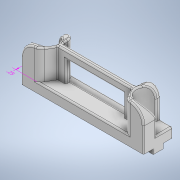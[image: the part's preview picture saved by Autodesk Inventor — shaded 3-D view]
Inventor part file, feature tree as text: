
AUTODESK INVENTOR PART (.ipt)
format: ipt  version: 2020 (Build 240168000, 168)  size: 448,512 bytes
history: native  units: in
note: dims shown in document units (in); Inventor stores cm internally (conversion verified against a paired STEP export)
features: fillet x8, sketch x6, extrude x5, other x2, hole x1
ambient origin geometry x8: Origin, YZ Plane, XZ Plane, XY Plane, X Axis, Y Axis, Z Axis, Center Point
bodies: Solid1 (feature_tree)
feature tree (22):
  other  "Annotations"
  extrude  "Extrusion1"  Depth=0.6in
  extrude  "Extrusion5"  Depth=0.1in
  extrude  "Extrusion8"  Depth=2.5in
  hole  "Hole3"  [1 undecoded]
  extrude  "Extrusion9"  Depth=0.5in
  extrude  "Extrusion10"  Depth=0.03in
  fillet  "Fillet3"  Radius=0.25in
  fillet  "Fillet4"  Radius=0.6in
  fillet  "Fillet5"  [1 undecoded]
  fillet  "Fillet6"  [1 undecoded]
  fillet  "Fillet7"  Radius=0.16in
  fillet  "Fillet8"  Radius=1.18in
  fillet  "Fillet9"  Radius=0.44in
  fillet  "Fillet10"  Radius=0.1in
  sketch  "Sketch1"  dims[d0=2.5in d1=0.6in]
  sketch  "Sketch6"  dims[d2=0.2in d3=0.0in d27=0.1in]
  sketch  "Sketch13"  dims[d28=0.2in d29=2.5in]
  sketch  "Sketch15"  dims[d30=0.2in d31=0.1in d32=0.0in]
  sketch  "Sketch16"  dims[d61=0.5in d62=0.5in]
  sketch  "Sketch18"  dims[d63=0.05in d64=0.1in d65=0.25in d66=0.6in d67=0.0in d68=60.0deg d69=120.0deg d70=0.2in d71=0.75in d72=0.4in d73=0.6in d74=0.5635in d75=1.0in d76=0.8108in d77=0.16in d78=1.18in d79=0.44in d80=0.1in d81=0.0in d89=0.12in d90=0.25in d91=0.0in d92=0.03in d93=0.03in d94=0.15in d95=0.3in d96=0.2in d97=0.03in d98=0.03in d99=0.03in d86=0.069in d87=0.3069in d88=0.25in d14=1.0in d15=1.0in d16=1.0in d17=0.15in d18=0.25in d19=0.375in d20=0.5635in d21=0.75in d22=0.8108in d23=0.0625in d24=0.75in d25=0.375in]
  other  "Linear Dimension 1"
note: 3 required parameter values undecoded (feature->parameter linkage not recoverable at this tier; creation-order binding heuristic only, values carry confidence <= 0.55)
